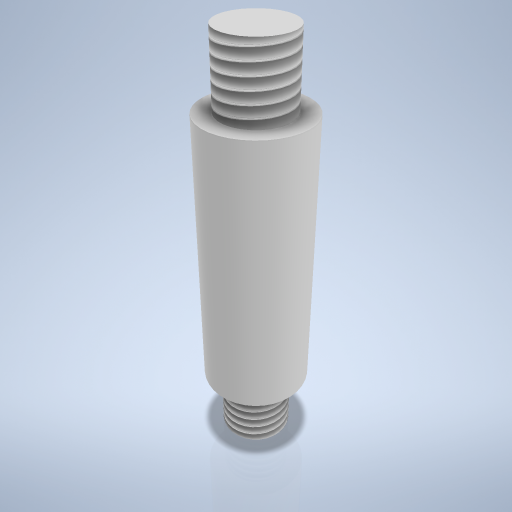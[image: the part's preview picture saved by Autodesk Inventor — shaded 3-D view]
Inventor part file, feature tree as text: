
AUTODESK INVENTOR PART (.ipt)
format: ipt  version: 2024.2 (Build 282272000, 272)  size: 265,216 bytes
history: native  units: mm
features: revolve x1, thread x1, sketch x1
ambient origin geometry x8: Origin, YZ Plane, XZ Plane, XY Plane, X Axis, Y Axis, Z Axis, Center Point
bodies: Volumenkörper1 (feature_tree)
feature tree (3):
  revolve  "Umdrehung1"
  thread  "Gewinde1"  [1 undecoded]
  sketch  "Skizze1"  dims[d1=32.0mm d2=8.0mm d3=8.0mm d4=12.0mm d5=90.0deg d6=48.0mm d7=0.0mm]
note: 1 required parameter value undecoded (feature->parameter linkage not recoverable at this tier; creation-order binding heuristic only, values carry confidence <= 0.55)
